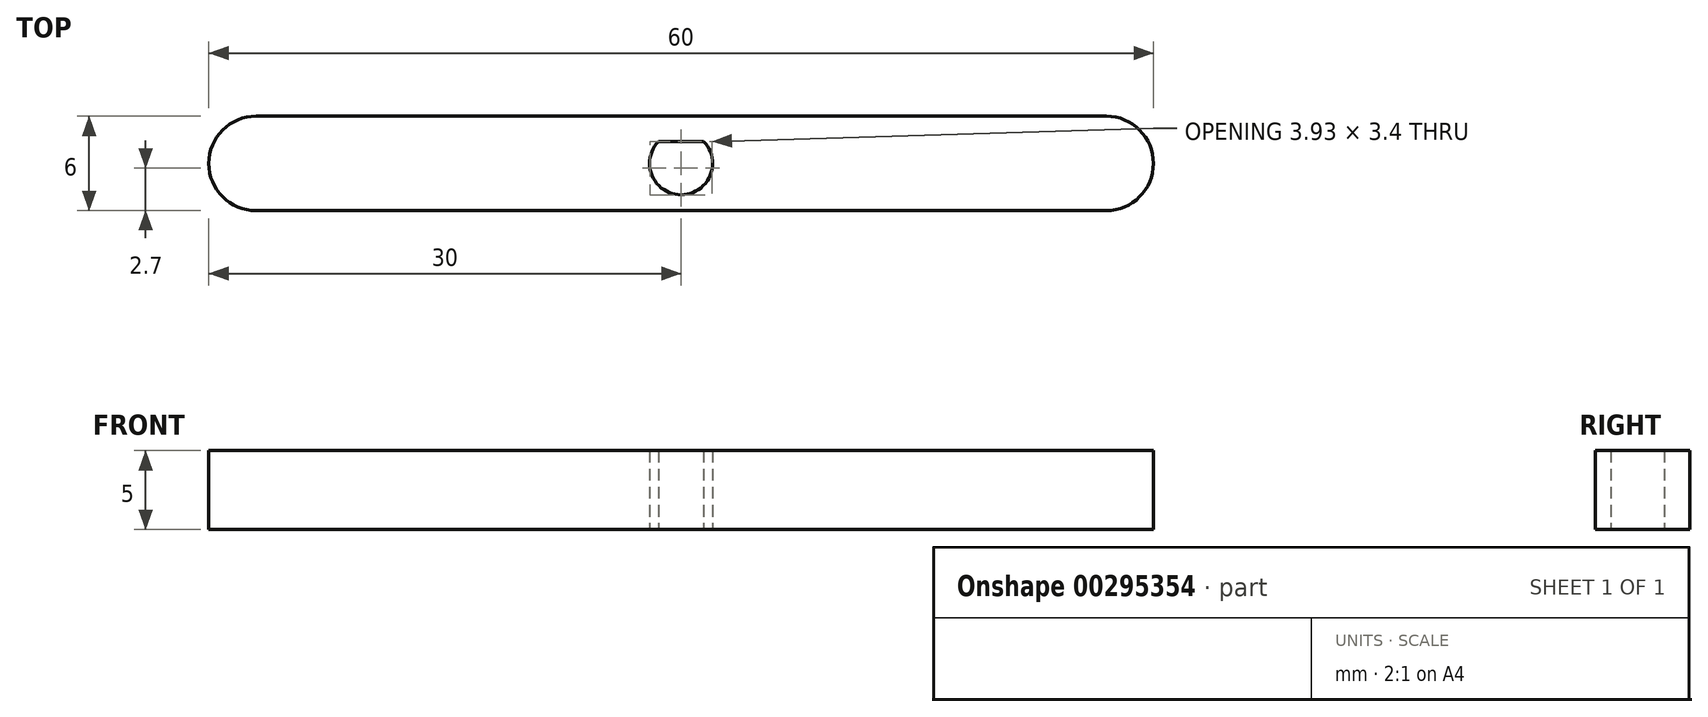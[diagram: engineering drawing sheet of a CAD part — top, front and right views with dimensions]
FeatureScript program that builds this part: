
annotation { "Feature Type Name" : "Feature", "Feature Type Description" : "" }
export const myFeature = defineFeature(function(context is Context, id is Id, definition is map)
    precondition{}
    {
        {
            var Q0;
            Q0=qCreatedBy(makeId("Top.planeOp"),FACE);
            var sketch = newSketch(context, id + "F0", { "sketchPlane" : qUnion([Q0])});
            skLineSegment(sketch, "E0.bottom", {"start": v(27, -3) * mm, "end": v(-27, -3) * mm});
            skLineSegment(sketch, "E0.top", {"start": v(27, 3) * mm, "end": v(-27, 3) * mm});
            skLineSegment(sketch, "E0.left", {"start": v(30, 0) * mm, "end": v(30, 0) * mm});
            skLineSegment(sketch, "E0.right", {"start": v(-30, 0) * mm, "end": v(-30, 0) * mm});
            skPoint(sketch, "E1.visualSharp", {"position": v(-30, 3) * mm});
            skArc(sketch, "E1.filletArc", {"start": v(-27, 3) * mm, "mid": v(-29.12, 2.12) * mm, "end": v(-30, 0) * mm});
            skPoint(sketch, "E2.visualSharp", {"position": v(-30, -3) * mm});
            skArc(sketch, "E2.filletArc", {"start": v(-30, 0) * mm, "mid": v(-29.12, -2.12) * mm, "end": v(-27, -3) * mm});
            skPoint(sketch, "E3.visualSharp", {"position": v(30, -3) * mm});
            skArc(sketch, "E3.filletArc", {"start": v(27, -3) * mm, "mid": v(29.12, -2.12) * mm, "end": v(30, 0) * mm});
            skPoint(sketch, "E4.visualSharp", {"position": v(30, 3) * mm});
            skArc(sketch, "E4.filletArc", {"start": v(30, 0) * mm, "mid": v(29.12, 2.12) * mm, "end": v(27, 3) * mm});
            skPoint(sketch, "E5", {"position": v(0, 0) * mm});
            skArc(sketch, "E6", {"start": v(-1.43, 1.4) * mm, "mid": v(0, -2) * mm, "end": v(1.43, 1.4) * mm});
            skLineSegment(sketch, "E7", {"start": v(-1.43, 1.4) * mm, "end": v(1.43, 1.4) * mm});
            skSolve(sketch);
        }
        {
            var Q0;
            Q0=makeQuery(id+"F0.imprint","IMPRINT",FACE,{"disambiguationData":[TD([[makeQuery(id+"F0.imprint","IMPRINT",EDGE,{"derivedFrom":sQuery(id+"F0.wireOp",EDGE,"E0.bottom")}),-1.0]])]});
            extrude(context, id + "F1", {"entities" : qUnion([Q0]), "depth" : 5 * mm});
        }
    });
